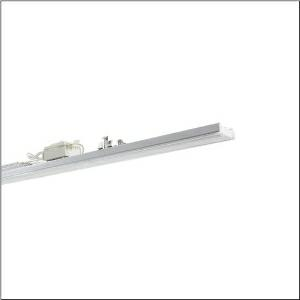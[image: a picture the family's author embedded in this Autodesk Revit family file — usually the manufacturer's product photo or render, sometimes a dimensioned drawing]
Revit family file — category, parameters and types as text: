
# Revit family: licross_21_recessed_mo_52tl18vn555g
name_source: partatom
category: Lighting Fixtures
units: mm (PartAtom-declared; Revit-internal decimal feet)

## family parameters
Cut with Voids When Loaded = No
Host = Face
Light Source = No
Part Type = Normal
Room Calculation Point = No
Round Connector Dimension = Use Diameter
Shared = No

## types (1)
- --- (1 x LED, 5500 lm, 30.9 W, 5000K)
    Apparent Load = 31 VA
    CIE Flux Codes = 79 95 99 100 100
    Color Rendering = 80
    Color Temperature = 5000K
    Default Elevation = 1800 mm
    Description = Licross 21 Recessed MO, luminaire insert, of sheet steel, galvanised, coil coated, white, length: 1.500mm, width: 66mm, height: 67mm, LED rated luminous flux: 5.500lm, light colour: 850, SDCM (Standard Deviation of Colour Matching)MacAdam ≤ 3 SDCM (initial), control gear: DALI 2, CLO, with plug, 5-pole, with phase selection, mains connection: 220..240V, AC, 50/60Hz, start of lifetime: 31W, end of service life: 37W, internal wiring halogen-free, primary optical cover: cover, of PMMA, light emission: direct distribution, primary light characteristic: symmetric, protection rating (complete): IP40, insulation class (complete): insulation class I (protective earthing), certification: CE, ENEC, VDE, UKCA, protection symbol: D if used in an environment without relevant dust loads with corresponding accessories, impact resistance: IK06, permissible ambient temperature for indoor applications: -25..+45°C, corresponds to IFS (International Featured Standards) requirements for safety and quality in the food industry, reducing of maximum allowable ambient temperature of 5°C with ceiling mounting, LABS conformity tested according to VDMA 24364:2018-05, The light source and the operating device comply with the requirements of the Ecodesign Regulation (EU) 2019/2020 and are replaceable in accordance with this regulation, packaging unit: 1 piece
    Height = 58 mm
    Lamp = 1 x LED
    Lamp Light Flux = 5500 lm
    Lamp Power = 30.9 W
    Lamp count = 1
    Length = 1500 mm
    Luminous efficacy = 178 lm/W
    Manufacturer = Siteco
    ModVariant = No
    Model = 52TL18VN555G
    Mounting Place = Ceiling
    Mounting Type = Pendant
    Number of Poles = 1
    OnlyDefault = Yes
    Power Factor = 1
    Product Name = Licross 21 Recessed MO
    Product group = luminaire insert | ceiling pendant
    ProductGroupID = 901
    Protection Class = Protection class I
    Protection Degree = IP 40
    RLX_Detail_Level = 1
    RLX_Emergency_Light_Flux = 0 lm
    RLX_Emergency_Type = 0
    RLX_Emergency_Type_DB = No
    RlxData = <blob elided: 24237 chars, md5=3db54268>
    Socket = socket
    Standby Power = 0 W
    System Light Flux = 5500 lm
    System Power = 31 W
    Type Comments = factory setting: luminous flux: 100 % | dim-lin: 254 | 209 mA
    Type Image = l_1296930.jpg
    URL = http://relux.com
    VarID = @adj_087125
    Voltage = 0 V
    Weight = 0.00 kg
    Width = 66 mm

## geometry (parser evidence)
native form markers: Blend x4, Sweep x11
no freeform markers — native parametric forms only
